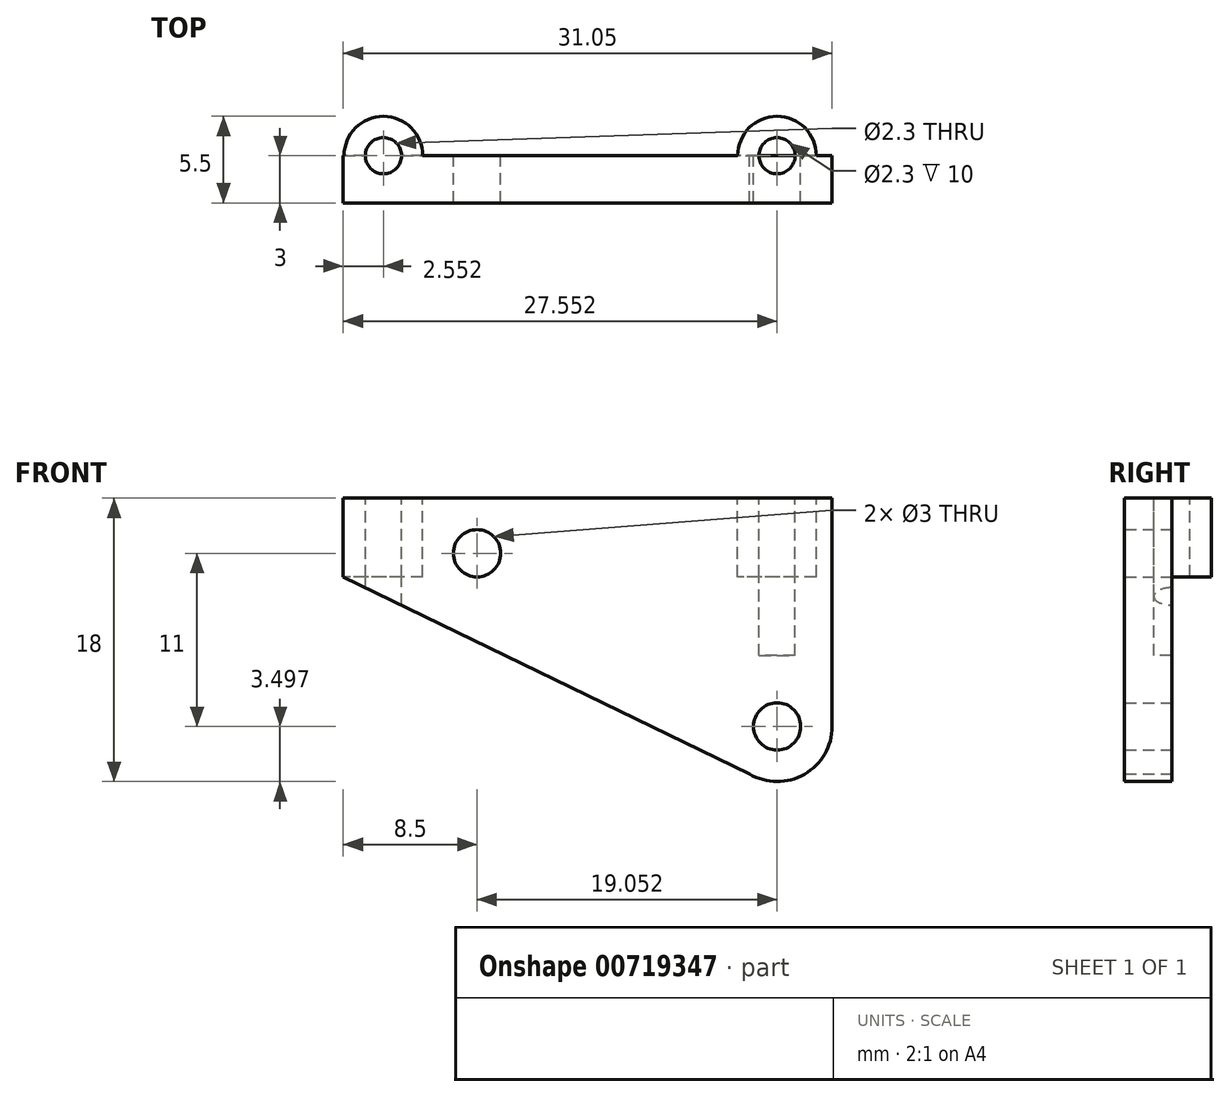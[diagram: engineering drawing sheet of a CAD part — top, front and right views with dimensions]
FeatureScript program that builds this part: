
annotation { "Feature Type Name" : "Feature", "Feature Type Description" : "" }
export const myFeature = defineFeature(function(context is Context, id is Id, definition is map)
    precondition{}
    {
        {
            var Q0;
            Q0=qCreatedBy(makeId("Front.planeOp"),FACE);
            var sketch = newSketch(context, id + "F0", { "sketchPlane" : qUnion([Q0])});
            skCircle(sketch, "E0", {"center": v(-7.35, 20.59) * mm, "radius": 1.5 * mm});
            skArc(sketch, "E1", {"start": v(10.4, 10.34) * mm, "mid": v(10.95, 8.29) * mm, "end": v(13, 8.84) * mm});
            skCircle(sketch, "E2", {"center": v(11.7, 9.59) * mm, "radius": 1.5 * mm});
            skArc(sketch, "E3", {"start": v(9.94, 6.56) * mm, "mid": v(13.45, 6.55) * mm, "end": v(15.2, 9.59) * mm});
            skLineSegment(sketch, "E4", {"start": v(15.2, 9.59) * mm, "end": v(15.2, 24.09) * mm});
            skLineSegment(sketch, "E5", {"start": v(-10.85, 24.09) * mm, "end": v(15.2, 24.09) * mm});
            skLineSegment(sketch, "E6", {"start": v(-10.85, 24.09) * mm, "end": v(-15.85, 24.09) * mm});
            skLineSegment(sketch, "E7", {"start": v(-15.85, 24.09) * mm, "end": v(-15.85, 19.09) * mm});
            skLineSegment(sketch, "E8", {"start": v(-15.85, 19.09) * mm, "end": v(9.94, 6.56) * mm});
            skSolve(sketch);
        }
        {
            var Q0;
            Q0=makeQuery(id+"F0.imprint","IMPRINT",FACE,{"disambiguationData":[TD([[makeQuery(id+"F0.imprint","IMPRINT",EDGE,{"derivedFrom":sQuery(id+"F0.wireOp",EDGE,"E0")}),-1.0]])]});
            extrude(context, id + "F1", {"entities" : qUnion([Q0]), "depth" : 3 * mm, "offsetDistance" : 25 * mm});
        }
        {
            var Q0;
            Q0=makeQuery(id+"F1.opExtrude","SWEPT_FACE",FACE,{"disambiguationData":[OSD([sQuery(id+"F0.wireOp",EDGE,"E5")])]});
            var sketch = newSketch(context, id + "F2", { "sketchPlane" : qUnion([Q0])});
            skCircle(sketch, "E9", {"center": v(11.7, 0) * mm, "radius": 2.5 * mm});
            skCircle(sketch, "E10", {"center": v(-13.3, 0) * mm, "radius": 2.5 * mm});
            skSolve(sketch);
        }
        {
            var Q0;
            Q0 = qSketchRegion(id + "F2", true);
            extrude(context, id + "F3", {"entities" : qUnion([Q0]), "operationType" : NewBodyOperationType.ADD, "oppositeDirection" : true, "depth" : 5 * mm, "offsetDistance" : 25 * mm});
        }
        {
            var Q0;
            Q0=makeQuery(id+"F3.boolean.opBoolean","MERGE",FACE,{"derivedFrom":[makeQuery(id+"F1.opExtrude","SWEPT_FACE",FACE,{"disambiguationData":[OSD([sQuery(id+"F0.wireOp",EDGE,"E5")])]}),makeQuery(id+"F3.opExtrude","CAP_FACE",FACE,{"disambiguationData":[OSD([sQuery(id+"F2.wireOp",EDGE,"E9")])],"isStart":true}),makeQuery(id+"F3.opExtrude","CAP_FACE",FACE,{"disambiguationData":[OSD([sQuery(id+"F2.wireOp",EDGE,"E10")])],"isStart":true})]});
            var sketch = newSketch(context, id + "F4", { "sketchPlane" : qUnion([Q0])});
            skCircle(sketch, "E11", {"center": v(11.7, 0) * mm, "radius": 1.15 * mm});
            skCircle(sketch, "E12", {"center": v(-13.3, 0) * mm, "radius": 1.15 * mm});
            skSolve(sketch);
        }
        {
            var Q0;
            Q0 = qSketchRegion(id + "F4", true);
            extrude(context, id + "F5", {"entities" : qUnion([Q0]), "operationType" : NewBodyOperationType.REMOVE, "oppositeDirection" : true, "depth" : 10 * mm, "offsetDistance" : 25 * mm});
        }
    });
